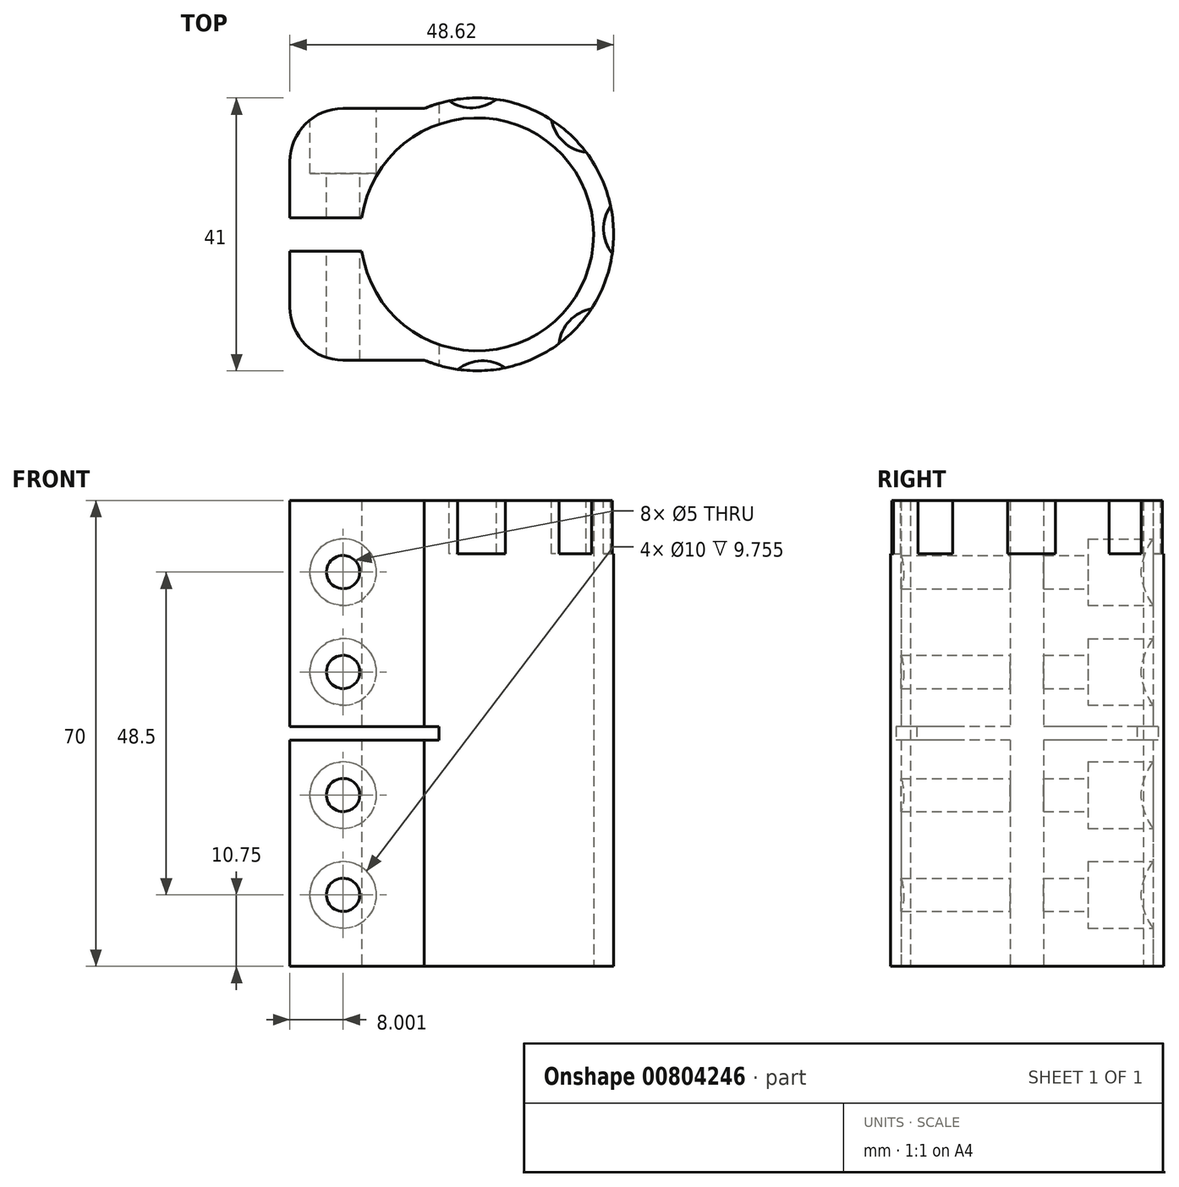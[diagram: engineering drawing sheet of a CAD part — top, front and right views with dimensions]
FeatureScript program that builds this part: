
annotation { "Feature Type Name" : "Feature", "Feature Type Description" : "" }
export const myFeature = defineFeature(function(context is Context, id is Id, definition is map)
    precondition{}
    {
        {
            var Q0;
            Q0=qCreatedBy(makeId("Top.planeOp"),FACE);
            var sketch = newSketch(context, id + "F0", { "sketchPlane" : qUnion([Q0])});
            skArc(sketch, "E0", {"start": v(-17.32, -2.5) * mm, "mid": v(17.5, 0) * mm, "end": v(-17.32, 2.5) * mm});
            skArc(sketch, "E1", {"start": v(-20.35, -2.5) * mm, "mid": v(17.73, -10.29) * mm, "end": v(-7.92, 18.9) * mm});
            skLineSegment(sketch, "E2", {"start": v(-7.92, 18.9) * mm, "end": v(-20.12, 18.9) * mm});
            skLineSegment(sketch, "E3", {"start": v(-28.12, 10.9) * mm, "end": v(-28.12, 2.5) * mm});
            skLineSegment(sketch, "E4", {"start": v(-28.12, 2.5) * mm, "end": v(-17.32, 2.5) * mm});
            skPoint(sketch, "E5.visualSharp", {"position": v(-28.12, 18.9) * mm});
            skArc(sketch, "E5.filletArc", {"start": v(-20.12, 18.9) * mm, "mid": v(-25.78, 16.57) * mm, "end": v(-28.12, 10.9) * mm});
            skLineSegment(sketch, "E6", {"start": v(0, 0) * mm, "end": v(55.32, 0) * mm, "construction": true});
            skLineSegment(sketch, "E7.MirrorCS", {"start": v(-28.12, -2.5) * mm, "end": v(-17.32, -2.5) * mm});
            skLineSegment(sketch, "E8.MirrorCS", {"start": v(-28.12, -10.9) * mm, "end": v(-28.12, -2.5) * mm});
            skArc(sketch, "E9.MirrorCS", {"start": v(-20.12, -18.9) * mm, "mid": v(-25.78, -16.57) * mm, "end": v(-28.12, -10.9) * mm});
            skLineSegment(sketch, "E10.MirrorCS", {"start": v(-7.92, -18.9) * mm, "end": v(-20.12, -18.9) * mm});
            skSolve(sketch);
        }
        {
            var Q0;
            {var subQ5=sQuery(id+"F0.wireOp",EDGE,"E0");Q0=makeQuery(id+"F0.imprint","IMPRINT",FACE,{"disambiguationData":[TD([[makeQuery(id+"F0.imprint","IMPRINT",EDGE,{"derivedFrom":subQ5}),-1.0]])]});}
            var Q1;
            {var subQ0=sQuery(id+"F0.wireOp",EDGE,"E8.MirrorCS");Q1=makeQuery(id+"F0.imprint","IMPRINT",FACE,{"disambiguationData":[TD([[makeQuery(id+"F0.imprint","IMPRINT",EDGE,{"derivedFrom":subQ0}),-1.0]])]});}
            extrude(context, id + "F1", {"entities" : qUnion([Q0, Q1]), "endBound" : BoundingType.SYMMETRIC, "depth" : 70 * mm, "offsetDistance" : 25 * mm});
        }
        {
            var Q0;
            Q0=makeQuery(id+"F1.opExtrude","SWEPT_FACE",FACE,{"disambiguationData":[OSD([sQuery(id+"F0.wireOp",EDGE,"E2")])]});
            var sketch = newSketch(context, id + "F2", { "sketchPlane" : qUnion([Q0])});
            skPoint(sketch, "E11", {"position": v(20.12, 24.25) * mm});
            skPoint(sketch, "E12", {"position": v(20.12, 9.25) * mm});
            skPoint(sketch, "E13", {"position": v(20.12, -9.25) * mm});
            skPoint(sketch, "E14", {"position": v(20.12, -24.25) * mm});
            skSolve(sketch);
        }
        {
            var Q0;
            Q0=sQuery(id+"F2.wireOp",VERTEX,"E11");
            var Q1;
            Q1=sQuery(id+"F2.wireOp",VERTEX,"E12");
            var Q2;
            Q2=sQuery(id+"F2.wireOp",VERTEX,"E13");
            var Q3;
            Q3=sQuery(id+"F2.wireOp",VERTEX,"E14");
            var Q4;
            Q4=makeQuery(id+"F1.opExtrude","SWEPT_BODY",BODY,{"disambiguationData":[OSD([sQuery(id+"F0.wireOp",EDGE,"E0"),sQuery(id+"F0.wireOp",EDGE,"E1"),sQuery(id+"F0.wireOp",EDGE,"E2"),sQuery(id+"F0.wireOp",EDGE,"E3"),sQuery(id+"F0.wireOp",EDGE,"E4"),sQuery(id+"F0.wireOp",EDGE,"E5.filletArc"),sQuery(id+"F0.wireOp",EDGE,"E7.MirrorCS"),sQuery(id+"F0.wireOp",EDGE,"E8.MirrorCS"),sQuery(id+"F0.wireOp",EDGE,"E9.MirrorCS"),sQuery(id+"F0.wireOp",EDGE,"E10.MirrorCS")])]});
            hole(context, id + "F3", {"style" : HoleStyle.C_BORE, "endStyle" : HoleEndStyle.THROUGH, "holeDiameter" : 5 * mm, "cBoreDiameter" : 10 * mm, "cBoreDepth" : 8 * mm, "majorDiameter" : 5 * mm, "isTappedThrough" : true, "tappedDepth" : 12 * mm, "tapClearance" : 3, "locations" : qUnion([Q0, Q1, Q2, Q3]), "scope" : qUnion([Q4])});
        }
        {
            var Q0;
            Q0=qCreatedBy(makeId("Front.planeOp"),FACE);
            var sketch = newSketch(context, id + "F4", { "sketchPlane" : qUnion([Q0])});
            skLineSegment(sketch, "E15.bottom", {"start": v(-5.72, 1) * mm, "end": v(-28.12, 1) * mm});
            skLineSegment(sketch, "E15.top", {"start": v(-5.72, -1) * mm, "end": v(-28.12, -1) * mm});
            skLineSegment(sketch, "E15.left", {"start": v(-5.72, 1) * mm, "end": v(-5.72, -1) * mm});
            skLineSegment(sketch, "E15.right", {"start": v(-28.12, 1) * mm, "end": v(-28.12, -1) * mm});
            skSolve(sketch);
        }
        {
            var Q0;
            Q0 = qSketchRegion(id + "F4", true);
            extrude(context, id + "F5", {"entities" : qUnion([Q0]), "operationType" : NewBodyOperationType.REMOVE, "endBound" : BoundingType.SYMMETRIC, "oppositeDirection" : true, "depth" : 50 * mm, "offsetDistance" : 25 * mm});
        }
        {
            var Q0;
            Q0=makeQuery(id+"F1.opExtrude","CAP_FACE",FACE,{"disambiguationData":[OSD([sQuery(id+"F0.wireOp",EDGE,"E0"),sQuery(id+"F0.wireOp",EDGE,"E1"),sQuery(id+"F0.wireOp",EDGE,"E2"),sQuery(id+"F0.wireOp",EDGE,"E3"),sQuery(id+"F0.wireOp",EDGE,"E4"),sQuery(id+"F0.wireOp",EDGE,"E5.filletArc"),sQuery(id+"F0.wireOp",EDGE,"E7.MirrorCS"),sQuery(id+"F0.wireOp",EDGE,"E8.MirrorCS"),sQuery(id+"F0.wireOp",EDGE,"E9.MirrorCS"),sQuery(id+"F0.wireOp",EDGE,"E10.MirrorCS")])],"isStart":false});
            var sketch = newSketch(context, id + "F6", { "sketchPlane" : qUnion([Q0])});
            skCircle(sketch, "E16", {"center": v(0.83, -25) * mm, "radius": 6 * mm});
            skCircle(sketch, "E17.1.0", {"center": v(18.26, -17.1) * mm, "radius": 6 * mm});
            skCircle(sketch, "E17.2.0", {"center": v(25, 0.83) * mm, "radius": 6 * mm});
            skCircle(sketch, "E17.3.0", {"center": v(17.1, 18.26) * mm, "radius": 6 * mm});
            skCircle(sketch, "E17.4.0", {"center": v(-0.83, 25) * mm, "radius": 6 * mm});
            skPoint(sketch, "E17.center", {"position": v(0, 0) * mm});
            skLineSegment(sketch, "E17.anchor1", {"start": v(0, 0) * mm, "end": v(0.83, -25) * mm, "construction": true});
            skLineSegment(sketch, "E17.anchor2", {"start": v(0, 0) * mm, "end": v(-0.83, 25) * mm, "construction": true});
            skSolve(sketch);
        }
        {
            var Q0;
            Q0 = qSketchRegion(id + "F6", true);
            extrude(context, id + "F7", {"entities" : qUnion([Q0]), "operationType" : NewBodyOperationType.REMOVE, "oppositeDirection" : true, "depth" : 8 * mm, "offsetDistance" : 25 * mm});
        }
    });
